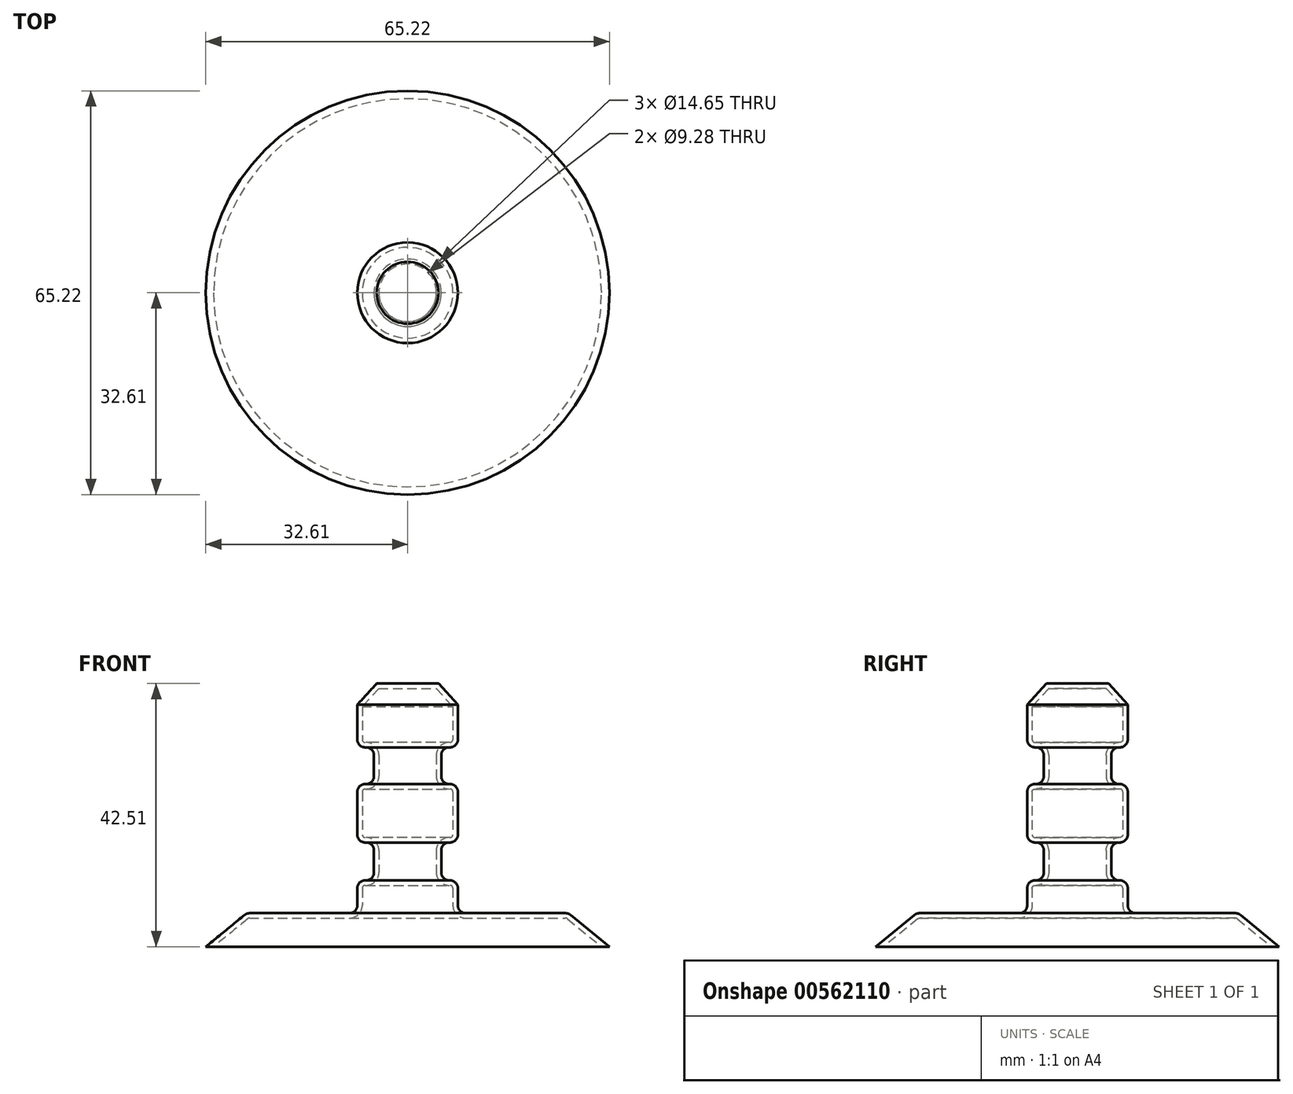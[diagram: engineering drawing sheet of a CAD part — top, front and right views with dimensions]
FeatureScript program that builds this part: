
annotation { "Feature Type Name" : "Feature", "Feature Type Description" : "" }
export const myFeature = defineFeature(function(context is Context, id is Id, definition is map)
    precondition{}
    {
        {
            var Q0;
            Q0=qCreatedBy(makeId("Front.planeOp"),FACE);
            var sketch = newSketch(context, id + "F0", { "sketchPlane" : qUnion([Q0])});
            skLineSegment(sketch, "E0", {"start": v(0, 0) * mm, "end": v(0, 42.5) * mm});
            skLineSegment(sketch, "E1", {"start": v(0, 42.5) * mm, "end": v(5, 42.5) * mm});
            skLineSegment(sketch, "E2", {"start": v(5, 42.5) * mm, "end": v(8.13, 39.07) * mm});
            skLineSegment(sketch, "E3", {"start": v(8.13, 39.07) * mm, "end": v(8.13, 32.2) * mm});
            skLineSegment(sketch, "E4", {"start": v(8.13, 32.2) * mm, "end": v(5.44, 32.2) * mm});
            skLineSegment(sketch, "E5", {"start": v(5.44, 32.2) * mm, "end": v(5.44, 26.27) * mm});
            skLineSegment(sketch, "E6", {"start": v(5.44, 26.27) * mm, "end": v(8.13, 26.27) * mm});
            skLineSegment(sketch, "E7", {"start": v(8.13, 26.27) * mm, "end": v(8.13, 16.83) * mm});
            skLineSegment(sketch, "E8", {"start": v(8.13, 16.83) * mm, "end": v(5.44, 16.83) * mm});
            skLineSegment(sketch, "E9", {"start": v(5.44, 16.83) * mm, "end": v(5.44, 10.7) * mm});
            skLineSegment(sketch, "E10", {"start": v(5.44, 10.7) * mm, "end": v(8.13, 10.7) * mm});
            skLineSegment(sketch, "E11", {"start": v(8.13, 10.7) * mm, "end": v(8.13, 5.4) * mm});
            skLineSegment(sketch, "E12", {"start": v(8.13, 5.4) * mm, "end": v(26, 5.4) * mm});
            skLineSegment(sketch, "E13", {"start": v(26, 5.4) * mm, "end": v(32.61, 0) * mm});
            skLineSegment(sketch, "E14", {"start": v(32.61, 0) * mm, "end": v(0, 0) * mm});
            skSolve(sketch);
        }
        {
            var Q0;
            Q0 = qSketchRegion(id + "F0", true);
            var Q1;
            Q1=sQuery(id+"F0.wireOp",EDGE,"E0");
            revolve(context, id + "F1", {"entities" : qUnion([Q0]), "axis" : qUnion([Q1]), "revolveType" : RevolveType.FULL});
        }
        {
            var Q0;
            Q0=makeQuery(id+"F1.opRevolve","SWEPT_EDGE",EDGE,{"disambiguationData":[OSD([sQuery(id+"F0.wireOp",EDGE,"E3"),sQuery(id+"F0.wireOp",EDGE,"E4")])]});
            var Q1;
            Q1=makeQuery(id+"F1.opRevolve","SWEPT_EDGE",EDGE,{"disambiguationData":[OSD([sQuery(id+"F0.wireOp",EDGE,"E6"),sQuery(id+"F0.wireOp",EDGE,"E7")])]});
            var Q2;
            Q2=makeQuery(id+"F1.opRevolve","SWEPT_EDGE",EDGE,{"disambiguationData":[OSD([sQuery(id+"F0.wireOp",EDGE,"E5"),sQuery(id+"F0.wireOp",EDGE,"E6")])]});
            var Q3;
            Q3=makeQuery(id+"F1.opRevolve","SWEPT_EDGE",EDGE,{"disambiguationData":[OSD([sQuery(id+"F0.wireOp",EDGE,"E4"),sQuery(id+"F0.wireOp",EDGE,"E5")])]});
            var Q4;
            Q4=makeQuery(id+"F1.opRevolve","SWEPT_EDGE",EDGE,{"disambiguationData":[OSD([sQuery(id+"F0.wireOp",EDGE,"E8"),sQuery(id+"F0.wireOp",EDGE,"E9")])]});
            var Q5;
            Q5=makeQuery(id+"F1.opRevolve","SWEPT_EDGE",EDGE,{"disambiguationData":[OSD([sQuery(id+"F0.wireOp",EDGE,"E7"),sQuery(id+"F0.wireOp",EDGE,"E8")])]});
            var Q6;
            Q6=makeQuery(id+"F1.opRevolve","SWEPT_EDGE",EDGE,{"disambiguationData":[OSD([sQuery(id+"F0.wireOp",EDGE,"E9"),sQuery(id+"F0.wireOp",EDGE,"E10")])]});
            var Q7;
            Q7=makeQuery(id+"F1.opRevolve","SWEPT_EDGE",EDGE,{"disambiguationData":[OSD([sQuery(id+"F0.wireOp",EDGE,"E10"),sQuery(id+"F0.wireOp",EDGE,"E11")])]});
            var Q8;
            Q8=makeQuery(id+"F1.opRevolve","SWEPT_EDGE",EDGE,{"disambiguationData":[OSD([sQuery(id+"F0.wireOp",EDGE,"E11"),sQuery(id+"F0.wireOp",EDGE,"E12")])]});
            var Q9;
            Q9=makeQuery(id+"F1.opRevolve","SWEPT_EDGE",EDGE,{"disambiguationData":[OSD([sQuery(id+"F0.wireOp",EDGE,"E12"),sQuery(id+"F0.wireOp",EDGE,"E13")])]});
            fillet(context, id + "F2", {"entities" : qUnion([Q0, Q1, Q2, Q3, Q4, Q5, Q6, Q7, Q8, Q9]), "radius" : 1.27 * mm, "tangentPropagation" : true, "allowEdgeOverflow" : false});
        }
        {
            var Q0;
            Q0=makeQuery(id+"F1.opRevolve","SWEPT_FACE",FACE,{"disambiguationData":[OSD([sQuery(id+"F0.wireOp",EDGE,"E14")])]});
            shell(context, id + "F3", {"entities" : qUnion([Q0]), "thickness" : .8 * mm});
        }
    });
